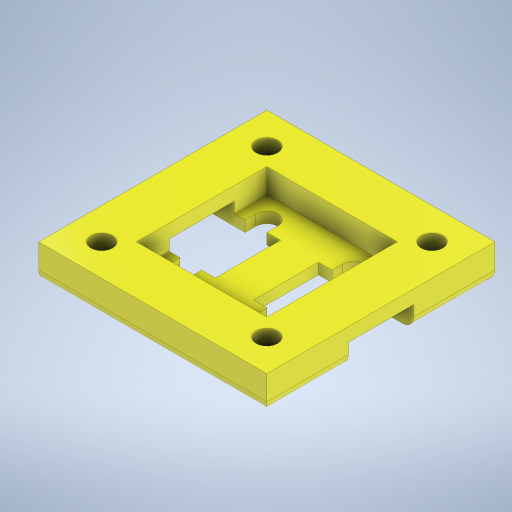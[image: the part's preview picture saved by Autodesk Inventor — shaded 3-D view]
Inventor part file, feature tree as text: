
AUTODESK INVENTOR PART (.ipt)
format: ipt  version: 2024 (Build 280153000, 153)  size: 384,512 bytes
history: native  units: mm
features: plane x9, extrude x7, projected_geometry x4, hole x2, fillet x1
ambient origin geometry x8: Origin, YZ Plane, XZ Plane, XY Plane, X Axis, Y Axis, Z Axis, Center Point
bodies: Solid1 (feature_tree)
feature tree (23):
  extrude  "Extrusion1"  Depth=42.0mm
  extrude  "Extrusion2"  Depth=42.0mm
  extrude  "Extrusion3"  Depth=6.5mm TaperAngle=0.0deg
  hole  "Hole1"  [1 undecoded]
  hole  "Hole2"  [1 undecoded]
  plane  "Work Plane5"
  plane  "Work Plane4"
  extrude  "Extrusion7"  Depth=4.5mm TaperAngle=0.0deg
  plane  "Work Plane6"
  extrude  "Extrusion8"  Depth=7.0mm
  plane  "Work Plane7"
  plane  "Work Plane8"
  plane  "Work Plane9"
  extrude  "Extrusion11"  Depth=12.0mm
  plane  "Work Plane10"
  plane  "Work Plane11"
  fillet  "Fillet4"  Radius=1.5mm
  plane  "Work Plane12"
  extrude  "Extrusion16"  Depth=7.0mm
  projected_geometry  "Projected Loop1"
  projected_geometry  "Projected Loop2"
  projected_geometry  "Projected Loop3"
  projected_geometry  "Projected Loop6"
note: 2 required parameter values undecoded (feature->parameter linkage not recoverable at this tier; creation-order binding heuristic only, values carry confidence <= 0.55)
